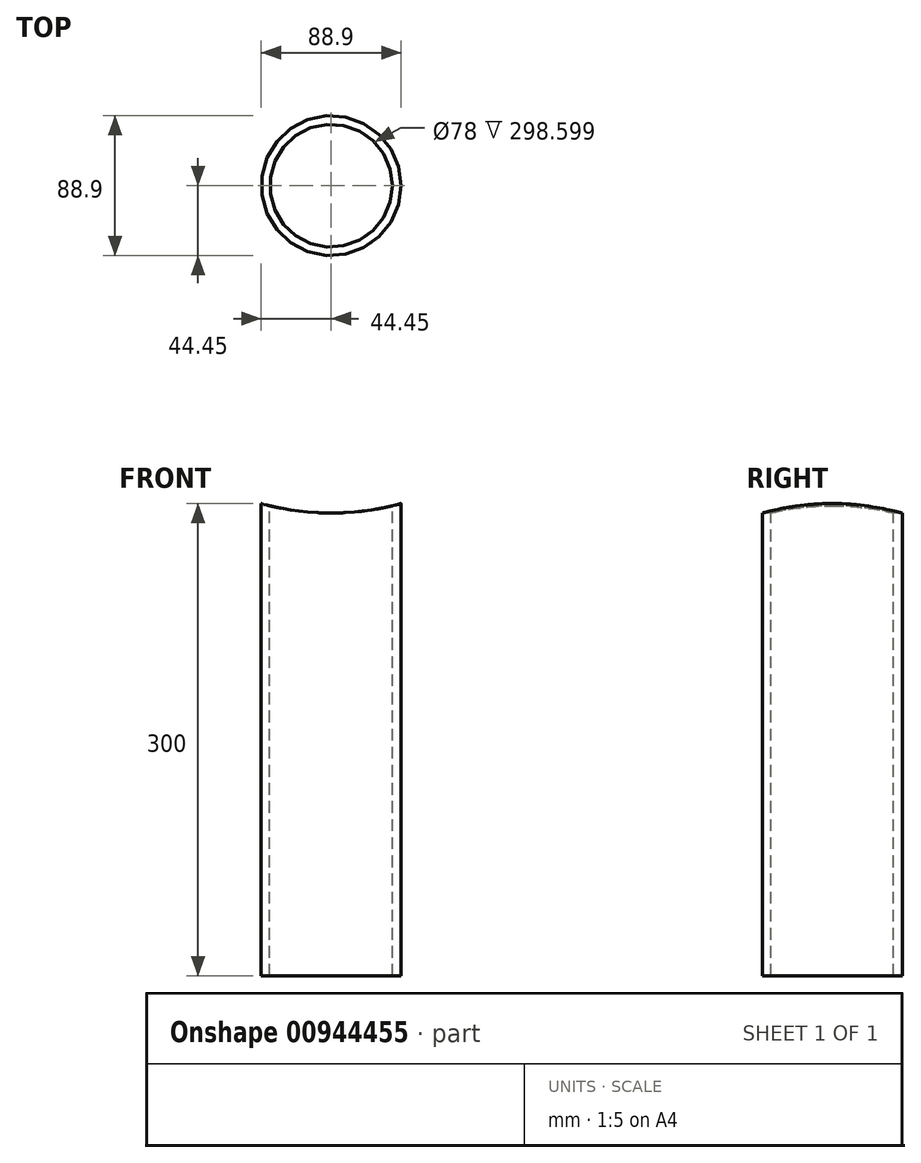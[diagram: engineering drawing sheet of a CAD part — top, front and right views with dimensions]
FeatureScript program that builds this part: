
annotation { "Feature Type Name" : "Feature", "Feature Type Description" : "" }
export const myFeature = defineFeature(function(context is Context, id is Id, definition is map)
    precondition{}
    {
        {
            var Q0;
            Q0=qCreatedBy(makeId("Top.planeOp"),FACE);
            var sketch = newSketch(context, id + "F0", { "sketchPlane" : qUnion([Q0])});
            skCircle(sketch, "E0", {"center": v(0, 0) * mm, "radius": 44.45 * mm});
            skCircle(sketch, "E1", {"center": v(0, 0) * mm, "radius": 39 * mm});
            skSolve(sketch);
        }
        {
            var Q0;
            Q0=makeQuery(id+"F0.imprint","IMPRINT",FACE,{"disambiguationData":[TD([[makeQuery(id+"F0.imprint","IMPRINT",EDGE,{"derivedFrom":sQuery(id+"F0.wireOp",EDGE,"E0")}),1.0]])]});
            extrude(context, id + "F1", {"entities" : qUnion([Q0]), "oppositeDirection" : true, "depth" : 300 * mm, "offsetDistance" : 25 * mm});
        }
        {
            var Q0;
            Q0=qCreatedBy(makeId("Front.planeOp"),FACE);
            var sketch = newSketch(context, id + "F2", { "sketchPlane" : qUnion([Q0])});
            skPoint(sketch, "E2", {"position": v(-44.45, 0) * mm});
            skPoint(sketch, "E3", {"position": v(44.45, 0) * mm});
            skLineSegment(sketch, "E4", {"start": v(-44.45, 0) * mm, "end": v(0, 161.5) * mm});
            skLineSegment(sketch, "E5", {"start": v(0, 161.5) * mm, "end": v(44.45, 0) * mm});
            skCircle(sketch, "E6", {"center": v(0, 161.5) * mm, "radius": 167.5 * mm});
            skSolve(sketch);
        }
        {
            var Q0;
            Q0 = qSketchRegion(id + "F2", true);
            extrude(context, id + "F3", {"entities" : qUnion([Q0]), "operationType" : NewBodyOperationType.REMOVE, "endBound" : BoundingType.THROUGH_ALL, "oppositeDirection" : true, "depth" : 25 * mm, "offsetDistance" : 25 * mm, "hasSecondDirection" : true, "secondDirectionBound" : SecondDirectionBoundingType.THROUGH_ALL, "secondDirectionOppositeDirection" : false, "secondDirectionDepth" : 25 * mm});
        }
    });
